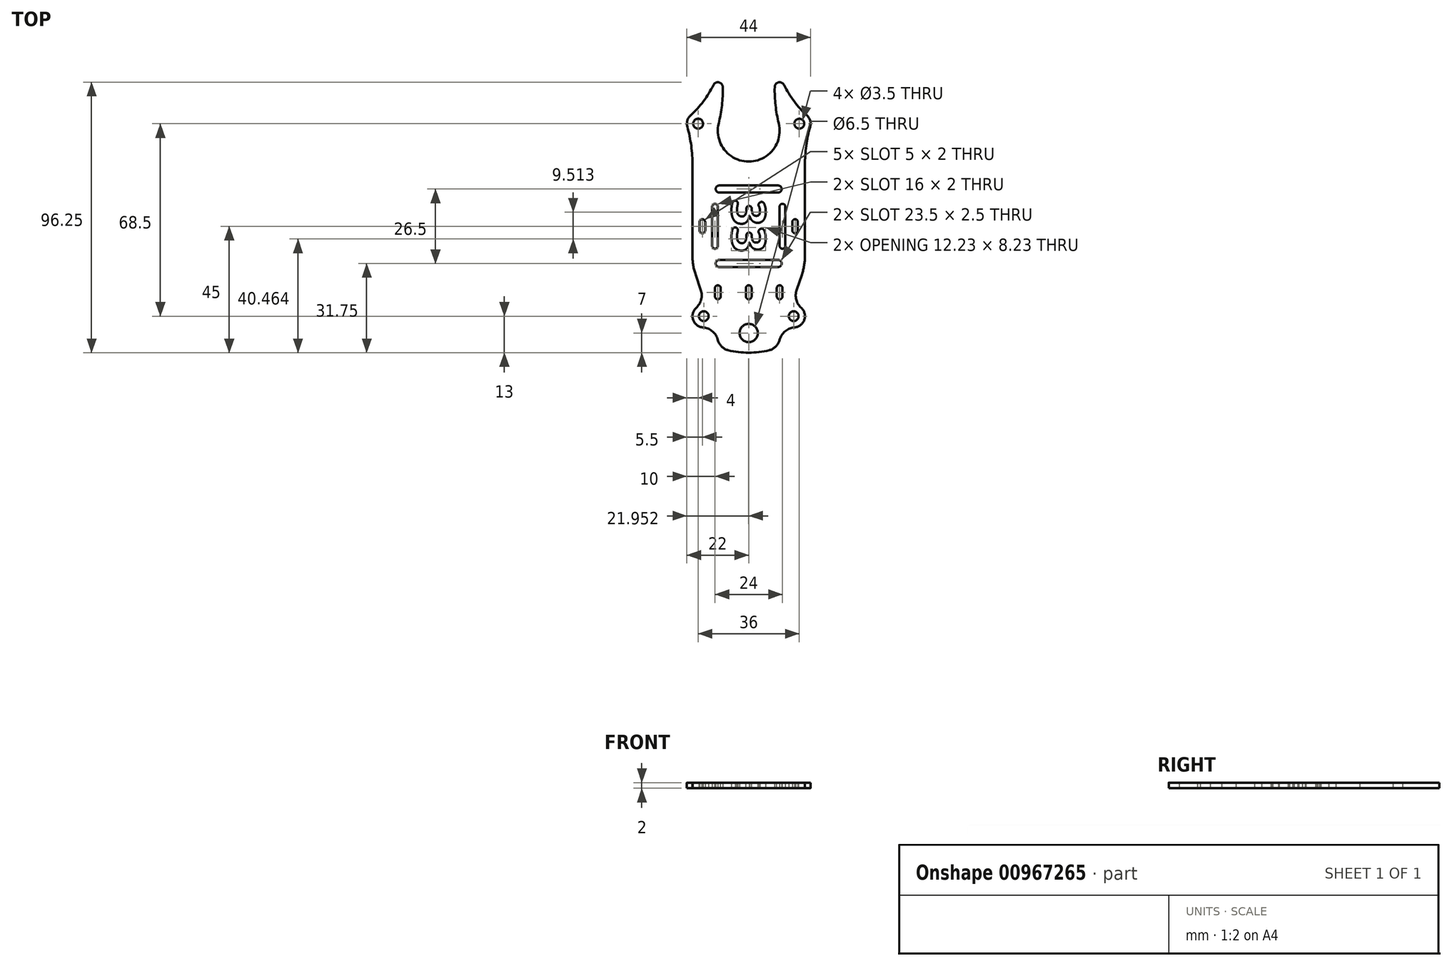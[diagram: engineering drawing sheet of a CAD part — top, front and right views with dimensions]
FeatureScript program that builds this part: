
annotation { "Feature Type Name" : "Feature", "Feature Type Description" : "" }
export const myFeature = defineFeature(function(context is Context, id is Id, definition is map)
    precondition{}
    {
        {
            var Q0;
            Q0=qCreatedBy(makeId("Top.planeOp"),FACE);
            var sketch = newSketch(context, id + "F0", { "sketchPlane" : qUnion([Q0])});
            skArc(sketch, "E0", {"start": v(-20.7, 39.46) * mm, "mid": v(-21.84, 37.62) * mm, "end": v(-21.86, 35.44) * mm});
            skLineSegment(sketch, "E1", {"start": v(-18.93, -17.14) * mm, "end": v(-17.05, -22.66) * mm});
            skArc(sketch, "E2", {"start": v(-10.68, 36.62) * mm, "mid": v(-8.66, 27.21) * mm, "end": v(0, 23) * mm});
            skLineSegment(sketch, "E3", {"start": v(0, 23) * mm, "end": v(0, -60) * mm, "construction": true});
            skCircle(sketch, "E4", {"center": v(-16, -32) * mm, "radius": 1.75 * mm});
            skArc(sketch, "E5.MirrorCS", {"start": v(10.68, 36.62) * mm, "mid": v(8.66, 27.21) * mm, "end": v(0, 23) * mm});
            skArc(sketch, "E6.MirrorCS", {"start": v(20.7, 39.46) * mm, "mid": v(21.84, 37.62) * mm, "end": v(21.86, 35.44) * mm});
            skCircle(sketch, "E7.MirrorC", {"center": v(16, -32) * mm, "radius": 1.75 * mm});
            skLineSegment(sketch, "E8.MirrorCS", {"start": v(18.93, -17.14) * mm, "end": v(17.05, -22.66) * mm});
            skCircle(sketch, "E9", {"center": v(-18, 36.5) * mm, "radius": 1.75 * mm});
            skCircle(sketch, "E10.MirrorC", {"center": v(18, 36.5) * mm, "radius": 1.75 * mm});
            skCircle(sketch, "E11", {"center": v(0, -38) * mm, "radius": 3.25 * mm});
            skArc(sketch, "E12", {"start": v(-7.28, -44.13) * mm, "mid": v(-3.66, -44.78) * mm, "end": v(0, -45) * mm});
            skLineSegment(sketch, "E13.trimOffspring", {"start": v(-20, 21.67) * mm, "end": v(-20, -10.69) * mm});
            skArc(sketch, "E14", {"start": v(16.32, -35.99) * mm, "mid": v(19.79, -33.3) * mm, "end": v(18.7, -29.04) * mm});
            skArc(sketch, "E15.filletArc", {"start": v(16.32, -35.99) * mm, "mid": v(13.12, -37.23) * mm, "end": v(11.13, -40.03) * mm});
            skArc(sketch, "E16.filletArc", {"start": v(17.05, -22.66) * mm, "mid": v(16.92, -26.1) * mm, "end": v(18.7, -29.04) * mm});
            skArc(sketch, "E17.MirrorCS", {"start": v(-16.32, -35.99) * mm, "mid": v(-13.12, -37.23) * mm, "end": v(-11.13, -40.03) * mm});
            skArc(sketch, "E18.MirrorCS", {"start": v(-16.32, -35.99) * mm, "mid": v(-19.79, -33.3) * mm, "end": v(-18.7, -29.04) * mm});
            skArc(sketch, "E19.MirrorCS", {"start": v(-17.05, -22.66) * mm, "mid": v(-16.92, -26.1) * mm, "end": v(-18.7, -29.04) * mm});
            skText(sketch, "E20", { "text": "33", "fontName": "OpenSans-Bold.ttf"});
            skLineSegment(sketch, "E21", {"start": v(-11.13, -40.03) * mm, "end": v(-10.84, -40.89) * mm});
            skLineSegment(sketch, "E22", {"start": v(11.13, -40.03) * mm, "end": v(10.84, -40.89) * mm});
            skLineSegment(sketch, "E23", {"start": v(-17.05, -22.66) * mm, "end": v(-11.13, -40.03) * mm, "construction": true});
            skLineSegment(sketch, "E24", {"start": v(17.05, -22.66) * mm, "end": v(11.13, -40.03) * mm, "construction": true});
            skArc(sketch, "E25", {"start": v(-9.25, 49.53) * mm, "mid": v(-10.62, 51.2) * mm, "end": v(-12.57, 50.27) * mm});
            skArc(sketch, "E26", {"start": v(-20.7, 39.46) * mm, "mid": v(-16.12, 44.48) * mm, "end": v(-12.57, 50.27) * mm});
            skArc(sketch, "E27.MirrorCS", {"start": v(9.25, 49.53) * mm, "mid": v(10.62, 51.2) * mm, "end": v(12.57, 50.27) * mm});
            skArc(sketch, "E28.MirrorCS", {"start": v(20.7, 39.46) * mm, "mid": v(16.12, 44.48) * mm, "end": v(12.57, 50.27) * mm});
            skPoint(sketch, "E29.visualSharp", {"position": v(-10, -43.34) * mm});
            skArc(sketch, "E29.filletArc", {"start": v(-10.84, -40.89) * mm, "mid": v(-9.47, -42.97) * mm, "end": v(-7.28, -44.13) * mm});
            skPoint(sketch, "E30.visualSharp", {"position": v(10, -43.34) * mm});
            skArc(sketch, "E30.filletArc", {"start": v(7.28, -44.13) * mm, "mid": v(9.47, -42.97) * mm, "end": v(10.84, -40.89) * mm});
            skLineSegment(sketch, "E31", {"start": v(-16.5, 1.5) * mm, "end": v(-16.5, -1.5) * mm, "construction": true});
            skArc(sketch, "E32.0.startCap", {"start": v(-17.5, 1.5) * mm, "mid": v(-16.5, 2.5) * mm, "end": v(-15.5, 1.5) * mm});
            skArc(sketch, "E32.0.endCap", {"start": v(-15.5, -1.5) * mm, "mid": v(-16.5, -2.5) * mm, "end": v(-17.5, -1.5) * mm});
            skLineSegment(sketch, "E32.0.left", {"start": v(-15.5, 1.5) * mm, "end": v(-15.5, -1.5) * mm});
            skLineSegment(sketch, "E32.0.right", {"start": v(-17.5, 1.5) * mm, "end": v(-17.5, -1.5) * mm});
            skLineSegment(sketch, "E33.MirrorCS", {"start": v(16.5, 1.5) * mm, "end": v(16.5, -1.5) * mm, "construction": true});
            skLineSegment(sketch, "E34.MirrorCS", {"start": v(15.5, 1.5) * mm, "end": v(15.5, -1.5) * mm});
            skLineSegment(sketch, "E35.MirrorCS", {"start": v(17.5, 1.5) * mm, "end": v(17.5, -1.5) * mm});
            skArc(sketch, "E36.MirrorCS", {"start": v(17.5, 1.5) * mm, "mid": v(16.5, 2.5) * mm, "end": v(15.5, 1.5) * mm});
            skArc(sketch, "E37.MirrorCS", {"start": v(15.5, -1.5) * mm, "mid": v(16.5, -2.5) * mm, "end": v(17.5, -1.5) * mm});
            skArc(sketch, "E38.filletArc", {"start": v(-10.68, 36.62) * mm, "mid": v(-9.55, 43.03) * mm, "end": v(-9.25, 49.53) * mm});
            skArc(sketch, "E39.filletArc", {"start": v(9.25, 49.53) * mm, "mid": v(9.55, 43.03) * mm, "end": v(10.68, 36.62) * mm});
            skArc(sketch, "E40", {"start": v(-20, 21.67) * mm, "mid": v(-20.47, 28.62) * mm, "end": v(-21.86, 35.44) * mm});
            skArc(sketch, "E41.MirrorCS", {"start": v(20, 21.67) * mm, "mid": v(20.47, 28.62) * mm, "end": v(21.86, 35.44) * mm});
            skCircle(sketch, "E42", {"center": v(0, -38) * mm, "radius": 4.5 * mm, "construction": true});
            skLineSegment(sketch, "E43", {"start": v(20, 21.67) * mm, "end": v(20, -10.69) * mm});
            skLineSegment(sketch, "E44", {"start": v(-10.5, 13.25) * mm, "end": v(10.5, 13.25) * mm, "construction": true});
            skLineSegment(sketch, "E45", {"start": v(-10.5, -13.25) * mm, "end": v(10.5, -13.25) * mm, "construction": true});
            skArc(sketch, "E46.0.startCap", {"start": v(-10.5, 12) * mm, "mid": v(-11.75, 13.25) * mm, "end": v(-10.5, 14.5) * mm});
            skArc(sketch, "E46.0.endCap", {"start": v(10.5, 14.5) * mm, "mid": v(11.75, 13.25) * mm, "end": v(10.5, 12) * mm});
            skLineSegment(sketch, "E46.0.left", {"start": v(-10.5, 14.5) * mm, "end": v(10.5, 14.5) * mm});
            skLineSegment(sketch, "E46.0.right", {"start": v(-10.5, 12) * mm, "end": v(10.5, 12) * mm});
            skArc(sketch, "E46.1.startCap", {"start": v(-10.5, -14.5) * mm, "mid": v(-11.75, -13.25) * mm, "end": v(-10.5, -12) * mm});
            skArc(sketch, "E46.1.endCap", {"start": v(10.5, -12) * mm, "mid": v(11.75, -13.25) * mm, "end": v(10.5, -14.5) * mm});
            skLineSegment(sketch, "E46.1.left", {"start": v(-10.5, -12) * mm, "end": v(10.5, -12) * mm});
            skLineSegment(sketch, "E46.1.right", {"start": v(-10.5, -14.5) * mm, "end": v(10.5, -14.5) * mm});
            skPoint(sketch, "E47.visualSharp", {"position": v(-20, -14) * mm});
            skArc(sketch, "E47.filletArc", {"start": v(-20, -10.69) * mm, "mid": v(-19.73, -13.96) * mm, "end": v(-18.93, -17.14) * mm});
            skPoint(sketch, "E48.visualSharp", {"position": v(20, -14) * mm});
            skArc(sketch, "E48.filletArc", {"start": v(18.93, -17.14) * mm, "mid": v(19.73, -13.96) * mm, "end": v(20, -10.69) * mm});
            skLineSegment(sketch, "E49", {"start": v(-12, 7) * mm, "end": v(-12, -7) * mm, "construction": true});
            skLineSegment(sketch, "E50.MirrorCS", {"start": v(12, 7) * mm, "end": v(12, -7) * mm, "construction": true});
            skArc(sketch, "E51.0.startCap", {"start": v(-13, 7) * mm, "mid": v(-12, 8) * mm, "end": v(-11, 7) * mm});
            skArc(sketch, "E51.0.endCap", {"start": v(-11, -7) * mm, "mid": v(-12, -8) * mm, "end": v(-13, -7) * mm});
            skLineSegment(sketch, "E51.0.left", {"start": v(-11, 7) * mm, "end": v(-11, -7) * mm});
            skLineSegment(sketch, "E51.0.right", {"start": v(-13, 7) * mm, "end": v(-13, -7) * mm});
            skArc(sketch, "E51.3.startCap", {"start": v(11, 7) * mm, "mid": v(12, 8) * mm, "end": v(13, 7) * mm});
            skArc(sketch, "E51.3.endCap", {"start": v(13, -7) * mm, "mid": v(12, -8) * mm, "end": v(11, -7) * mm});
            skLineSegment(sketch, "E51.3.left", {"start": v(13, 7) * mm, "end": v(13, -7) * mm});
            skLineSegment(sketch, "E51.3.right", {"start": v(11, 7) * mm, "end": v(11, -7) * mm});
            skPoint(sketch, "E52.startSnap0", {"position": v(-16.5, 2.5) * mm});
            skArc(sketch, "E53.trimOffspring", {"start": v(0, -45) * mm, "mid": v(3.66, -44.78) * mm, "end": v(7.28, -44.13) * mm});
            const initialGuessF0  = {"E20": [-0.006, 0.00973, 0, -1, 0.012]};
            skSetInitialGuess(sketch, initialGuessF0);
            skSolve(sketch);
        }
        {
            var Q0;
            Q0=qSketchRegion(id+"F0",true);
            extrude(context, id + "F1", {"entities" : qUnion([Q0]), "depth" : 2 * mm});
        }
        {
            var Q0;
            Q0=makeQuery(id+"F1.opExtrude","SWEPT_EDGE",EDGE,{"disambiguationData":[OSD([sQuery(id+"F0.wireOp",EDGE,"E20.sketch_text.stroke-23"),sQuery(id+"F0.wireOp",EDGE,"E20.sketch_text.stroke-24")])]});
            var Q1;
            Q1=makeQuery(id+"F1.opExtrude","SWEPT_EDGE",EDGE,{"disambiguationData":[OSD([sQuery(id+"F0.wireOp",EDGE,"E20.sketch_text.stroke-22"),sQuery(id+"F0.wireOp",EDGE,"E20.sketch_text.stroke-23")])]});
            var Q2;
            Q2=makeQuery(id+"F1.opExtrude","SWEPT_EDGE",EDGE,{"disambiguationData":[OSD([sQuery(id+"F0.wireOp",EDGE,"E20.sketch_text.stroke-16"),sQuery(id+"F0.wireOp",EDGE,"E20.sketch_text.stroke-17")])]});
            var Q3;
            Q3=makeQuery(id+"F1.opExtrude","SWEPT_EDGE",EDGE,{"disambiguationData":[OSD([sQuery(id+"F0.wireOp",EDGE,"E20.sketch_text.stroke-15"),sQuery(id+"F0.wireOp",EDGE,"E20.sketch_text.stroke-16")])]});
            var Q4;
            Q4=makeQuery(id+"F1.opExtrude","SWEPT_EDGE",EDGE,{"disambiguationData":[OSD([sQuery(id+"F0.wireOp",EDGE,"E20.sketch_text.stroke-8"),sQuery(id+"F0.wireOp",EDGE,"E20.sketch_text.stroke-9")])]});
            var Q5;
            Q5=makeQuery(id+"F1.opExtrude","SWEPT_EDGE",EDGE,{"disambiguationData":[OSD([sQuery(id+"F0.wireOp",EDGE,"E20.sketch_text.stroke-7"),sQuery(id+"F0.wireOp",EDGE,"E20.sketch_text.stroke-8")])]});
            var Q6;
            Q6=makeQuery(id+"F1.opExtrude","SWEPT_EDGE",EDGE,{"disambiguationData":[OSD([sQuery(id+"F0.wireOp",EDGE,"E20.sketch_text.stroke-35"),sQuery(id+"F0.wireOp",EDGE,"E20.sketch_text.stroke-36")])]});
            var Q7;
            Q7=makeQuery(id+"F1.opExtrude","SWEPT_EDGE",EDGE,{"disambiguationData":[OSD([sQuery(id+"F0.wireOp",EDGE,"E20.sketch_text.stroke-34"),sQuery(id+"F0.wireOp",EDGE,"E20.sketch_text.stroke-35")])]});
            var Q8;
            Q8=makeQuery(id+"F1.opExtrude","SWEPT_EDGE",EDGE,{"disambiguationData":[OSD([sQuery(id+"F0.wireOp",EDGE,"E20.sketch_text.stroke-42"),sQuery(id+"F0.wireOp",EDGE,"E20.sketch_text.stroke-43")])]});
            var Q9;
            Q9=makeQuery(id+"F1.opExtrude","SWEPT_EDGE",EDGE,{"disambiguationData":[OSD([sQuery(id+"F0.wireOp",EDGE,"E20.sketch_text.stroke-43"),sQuery(id+"F0.wireOp",EDGE,"E20.sketch_text.stroke-44")])]});
            var Q10;
            Q10=makeQuery(id+"F1.opExtrude","SWEPT_EDGE",EDGE,{"disambiguationData":[OSD([sQuery(id+"F0.wireOp",EDGE,"E20.sketch_text.stroke-49"),sQuery(id+"F0.wireOp",EDGE,"E20.sketch_text.stroke-50")])]});
            var Q11;
            Q11=makeQuery(id+"F1.opExtrude","SWEPT_EDGE",EDGE,{"disambiguationData":[OSD([sQuery(id+"F0.wireOp",EDGE,"E20.sketch_text.stroke-50"),sQuery(id+"F0.wireOp",EDGE,"E20.sketch_text.stroke-51")])]});
            fillet(context, id + "F2", {"entities" : qUnion([Q0, Q1, Q2, Q3, Q4, Q5, Q6, Q7, Q8, Q9, Q10, Q11]), "radius" : 1 * mm, "tangentPropagation" : true, "allowEdgeOverflow" : false});
        }
        {
            var Q0;
            Q0=makeQuery(id+"F1.opExtrude","CAP_FACE",FACE,{"disambiguationData":[OSD([sQuery(id+"F0.wireOp",EDGE,"E0"),sQuery(id+"F0.wireOp",EDGE,"E1"),sQuery(id+"F0.wireOp",EDGE,"E2"),sQuery(id+"F0.wireOp",EDGE,"E4"),sQuery(id+"F0.wireOp",EDGE,"E5.MirrorCS"),sQuery(id+"F0.wireOp",EDGE,"E6.MirrorCS"),sQuery(id+"F0.wireOp",EDGE,"E7.MirrorC"),sQuery(id+"F0.wireOp",EDGE,"E8.MirrorCS"),sQuery(id+"F0.wireOp",EDGE,"E9"),sQuery(id+"F0.wireOp",EDGE,"E10.MirrorC"),sQuery(id+"F0.wireOp",EDGE,"E11"),sQuery(id+"F0.wireOp",EDGE,"E12"),sQuery(id+"F0.wireOp",EDGE,"E13.trimOffspring"),sQuery(id+"F0.wireOp",EDGE,"E14"),sQuery(id+"F0.wireOp",EDGE,"E15.filletArc"),sQuery(id+"F0.wireOp",EDGE,"E16.filletArc"),sQuery(id+"F0.wireOp",EDGE,"E17.MirrorCS"),sQuery(id+"F0.wireOp",EDGE,"E18.MirrorCS"),sQuery(id+"F0.wireOp",EDGE,"E19.MirrorCS"),sQuery(id+"F0.wireOp",EDGE,"E20.sketch_text.stroke-0"),sQuery(id+"F0.wireOp",EDGE,"E20.sketch_text.stroke-1"),sQuery(id+"F0.wireOp",EDGE,"E20.sketch_text.stroke-2"),sQuery(id+"F0.wireOp",EDGE,"E20.sketch_text.stroke-3"),sQuery(id+"F0.wireOp",EDGE,"E20.sketch_text.stroke-4"),sQuery(id+"F0.wireOp",EDGE,"E20.sketch_text.stroke-5"),sQuery(id+"F0.wireOp",EDGE,"E20.sketch_text.stroke-6"),sQuery(id+"F0.wireOp",EDGE,"E20.sketch_text.stroke-7"),sQuery(id+"F0.wireOp",EDGE,"E20.sketch_text.stroke-8"),sQuery(id+"F0.wireOp",EDGE,"E20.sketch_text.stroke-9"),sQuery(id+"F0.wireOp",EDGE,"E20.sketch_text.stroke-10"),sQuery(id+"F0.wireOp",EDGE,"E20.sketch_text.stroke-11"),sQuery(id+"F0.wireOp",EDGE,"E20.sketch_text.stroke-12"),sQuery(id+"F0.wireOp",EDGE,"E20.sketch_text.stroke-13"),sQuery(id+"F0.wireOp",EDGE,"E20.sketch_text.stroke-14"),sQuery(id+"F0.wireOp",EDGE,"E20.sketch_text.stroke-15"),sQuery(id+"F0.wireOp",EDGE,"E20.sketch_text.stroke-16"),sQuery(id+"F0.wireOp",EDGE,"E20.sketch_text.stroke-17"),sQuery(id+"F0.wireOp",EDGE,"E20.sketch_text.stroke-18"),sQuery(id+"F0.wireOp",EDGE,"E20.sketch_text.stroke-19"),sQuery(id+"F0.wireOp",EDGE,"E20.sketch_text.stroke-20"),sQuery(id+"F0.wireOp",EDGE,"E20.sketch_text.stroke-21"),sQuery(id+"F0.wireOp",EDGE,"E20.sketch_text.stroke-22"),sQuery(id+"F0.wireOp",EDGE,"E20.sketch_text.stroke-23"),sQuery(id+"F0.wireOp",EDGE,"E20.sketch_text.stroke-24"),sQuery(id+"F0.wireOp",EDGE,"E20.sketch_text.stroke-25"),sQuery(id+"F0.wireOp",EDGE,"E20.sketch_text.stroke-26"),sQuery(id+"F0.wireOp",EDGE,"E20.sketch_text.stroke-27"),sQuery(id+"F0.wireOp",EDGE,"E20.sketch_text.stroke-28"),sQuery(id+"F0.wireOp",EDGE,"E20.sketch_text.stroke-29"),sQuery(id+"F0.wireOp",EDGE,"E20.sketch_text.stroke-30"),sQuery(id+"F0.wireOp",EDGE,"E20.sketch_text.stroke-31"),sQuery(id+"F0.wireOp",EDGE,"E20.sketch_text.stroke-32"),sQuery(id+"F0.wireOp",EDGE,"E20.sketch_text.stroke-33"),sQuery(id+"F0.wireOp",EDGE,"E20.sketch_text.stroke-34"),sQuery(id+"F0.wireOp",EDGE,"E20.sketch_text.stroke-35"),sQuery(id+"F0.wireOp",EDGE,"E20.sketch_text.stroke-36"),sQuery(id+"F0.wireOp",EDGE,"E20.sketch_text.stroke-37"),sQuery(id+"F0.wireOp",EDGE,"E20.sketch_text.stroke-38"),sQuery(id+"F0.wireOp",EDGE,"E20.sketch_text.stroke-39"),sQuery(id+"F0.wireOp",EDGE,"E20.sketch_text.stroke-40"),sQuery(id+"F0.wireOp",EDGE,"E20.sketch_text.stroke-41"),sQuery(id+"F0.wireOp",EDGE,"E20.sketch_text.stroke-42"),sQuery(id+"F0.wireOp",EDGE,"E20.sketch_text.stroke-43"),sQuery(id+"F0.wireOp",EDGE,"E20.sketch_text.stroke-44"),sQuery(id+"F0.wireOp",EDGE,"E20.sketch_text.stroke-45"),sQuery(id+"F0.wireOp",EDGE,"E20.sketch_text.stroke-46"),sQuery(id+"F0.wireOp",EDGE,"E20.sketch_text.stroke-47"),sQuery(id+"F0.wireOp",EDGE,"E20.sketch_text.stroke-48"),sQuery(id+"F0.wireOp",EDGE,"E20.sketch_text.stroke-49"),sQuery(id+"F0.wireOp",EDGE,"E20.sketch_text.stroke-50"),sQuery(id+"F0.wireOp",EDGE,"E20.sketch_text.stroke-51"),sQuery(id+"F0.wireOp",EDGE,"E20.sketch_text.stroke-52"),sQuery(id+"F0.wireOp",EDGE,"E20.sketch_text.stroke-53"),sQuery(id+"F0.wireOp",EDGE,"E21"),sQuery(id+"F0.wireOp",EDGE,"E22"),sQuery(id+"F0.wireOp",EDGE,"E25"),sQuery(id+"F0.wireOp",EDGE,"E26"),sQuery(id+"F0.wireOp",EDGE,"E27.MirrorCS"),sQuery(id+"F0.wireOp",EDGE,"E28.MirrorCS"),sQuery(id+"F0.wireOp",EDGE,"E29.filletArc"),sQuery(id+"F0.wireOp",EDGE,"E30.filletArc"),sQuery(id+"F0.wireOp",EDGE,"E32.0.startCap"),sQuery(id+"F0.wireOp",EDGE,"E32.0.endCap"),sQuery(id+"F0.wireOp",EDGE,"E32.0.left"),sQuery(id+"F0.wireOp",EDGE,"E32.0.right"),sQuery(id+"F0.wireOp",EDGE,"E34.MirrorCS"),sQuery(id+"F0.wireOp",EDGE,"E35.MirrorCS"),sQuery(id+"F0.wireOp",EDGE,"E36.MirrorCS"),sQuery(id+"F0.wireOp",EDGE,"E37.MirrorCS"),sQuery(id+"F0.wireOp",EDGE,"E38.filletArc"),sQuery(id+"F0.wireOp",EDGE,"E39.filletArc"),sQuery(id+"F0.wireOp",EDGE,"E40"),sQuery(id+"F0.wireOp",EDGE,"E41.MirrorCS"),sQuery(id+"F0.wireOp",EDGE,"E43"),sQuery(id+"F0.wireOp",EDGE,"E46.0.startCap"),sQuery(id+"F0.wireOp",EDGE,"E46.0.endCap"),sQuery(id+"F0.wireOp",EDGE,"E46.0.left"),sQuery(id+"F0.wireOp",EDGE,"E46.0.right"),sQuery(id+"F0.wireOp",EDGE,"E46.1.startCap"),sQuery(id+"F0.wireOp",EDGE,"E46.1.endCap"),sQuery(id+"F0.wireOp",EDGE,"E46.1.left"),sQuery(id+"F0.wireOp",EDGE,"E46.1.right"),sQuery(id+"F0.wireOp",EDGE,"E47.filletArc"),sQuery(id+"F0.wireOp",EDGE,"E48.filletArc"),sQuery(id+"F0.wireOp",EDGE,"E51.0.startCap"),sQuery(id+"F0.wireOp",EDGE,"E51.0.endCap"),sQuery(id+"F0.wireOp",EDGE,"E51.0.left"),sQuery(id+"F0.wireOp",EDGE,"E51.0.right"),sQuery(id+"F0.wireOp",EDGE,"E51.3.startCap"),sQuery(id+"F0.wireOp",EDGE,"E51.3.endCap"),sQuery(id+"F0.wireOp",EDGE,"E51.3.left"),sQuery(id+"F0.wireOp",EDGE,"E51.3.right"),sQuery(id+"F0.wireOp",EDGE,"E53.trimOffspring")])],"isStart":false});
            var sketch = newSketch(context, id + "F3", { "sketchPlane" : qUnion([Q0])});
            skLineSegment(sketch, "E54", {"start": v(11, -22) * mm, "end": v(11, -25) * mm});
            skLineSegment(sketch, "E55", {"start": v(0, -22) * mm, "end": v(0, -25) * mm});
            skArc(sketch, "E56.0.startCap", {"start": v(10, -22) * mm, "mid": v(11, -21) * mm, "end": v(12, -22) * mm});
            skArc(sketch, "E56.0.endCap", {"start": v(12, -25) * mm, "mid": v(11, -26) * mm, "end": v(10, -25) * mm});
            skLineSegment(sketch, "E56.0.left", {"start": v(12, -22) * mm, "end": v(12, -25) * mm});
            skLineSegment(sketch, "E56.0.right", {"start": v(10, -22) * mm, "end": v(10, -25) * mm});
            skArc(sketch, "E56.1.startCap", {"start": v(-1, -22) * mm, "mid": v(0, -21) * mm, "end": v(1, -22) * mm});
            skArc(sketch, "E56.1.endCap", {"start": v(1, -25) * mm, "mid": v(0, -26) * mm, "end": v(-1, -25) * mm});
            skLineSegment(sketch, "E56.1.left", {"start": v(1, -22) * mm, "end": v(1, -25) * mm});
            skLineSegment(sketch, "E56.1.right", {"start": v(-1, -22) * mm, "end": v(-1, -25) * mm});
            skLineSegment(sketch, "E57.MirrorCS", {"start": v(-10, -22) * mm, "end": v(-10, -25) * mm});
            skLineSegment(sketch, "E58.MirrorCS", {"start": v(-12, -22) * mm, "end": v(-12, -25) * mm});
            skLineSegment(sketch, "E59.MirrorCS", {"start": v(-11, -22) * mm, "end": v(-11, -25) * mm});
            skArc(sketch, "E60.MirrorCS", {"start": v(-10, -22) * mm, "mid": v(-11, -21) * mm, "end": v(-12, -22) * mm});
            skArc(sketch, "E61.MirrorCS", {"start": v(-12, -25) * mm, "mid": v(-11, -26) * mm, "end": v(-10, -25) * mm});
            skSolve(sketch);
        }
        {
            var Q0;
            Q0=qSketchRegion(id+"F3",true);
            extrude(context, id + "F4", {"entities" : qUnion([Q0]), "operationType" : NewBodyOperationType.REMOVE, "oppositeDirection" : true, "depth" : 25 * mm});
        }
    });
